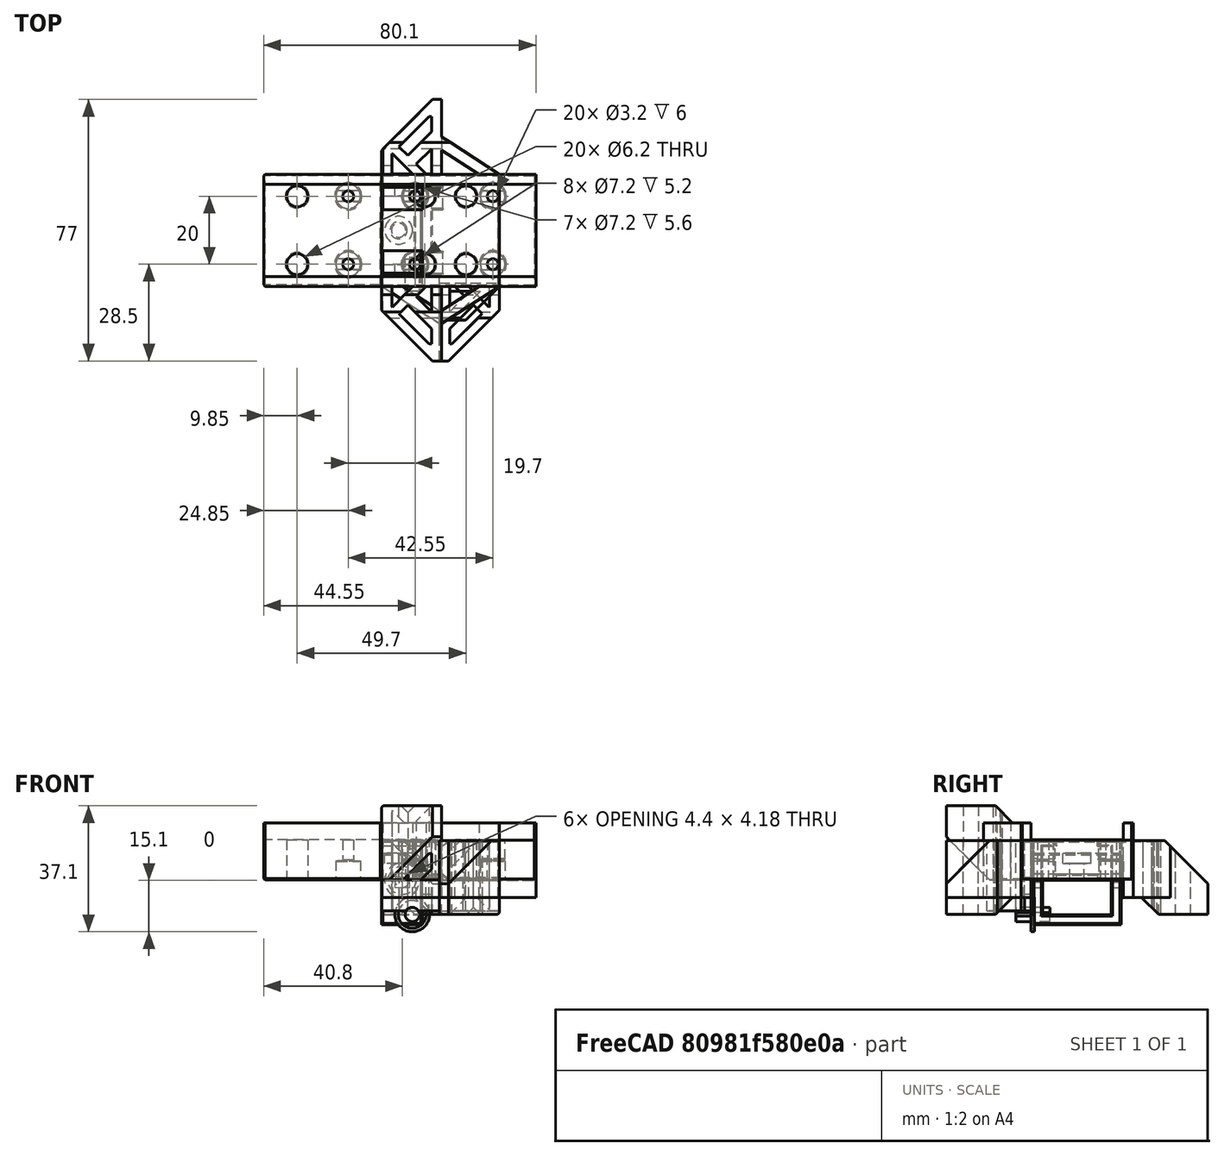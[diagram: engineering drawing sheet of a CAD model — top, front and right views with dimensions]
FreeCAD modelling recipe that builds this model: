
FCSTD DOCUMENT  (FreeCAD 0.18R14555 (Git shallow))
Label: bear-railt-mount
License: All rights reserved
LicenseURL: http://en.wikipedia.org/wiki/All_rights_reserved
objects: Part::Box×31, Part::Feature×25, Part::Cut×24, Part::Cylinder×22, Part::MultiFuse×16, Part::Chamfer×15, Part::MultiCommon×1
note: 134 computed .brp shape members not serialized (recipe doc carries the construction recipe); baked Part::Feature solids carry a one-line shape summary decoded from their .brp

FEATURE [Part::Box] Box  label="Cube"
  AttacherType = Attacher::AttachEngine3D
  Height = 2
  Length = 18
  Placement = pos=(0,-13,0) rot=(0,0,1;0rad)
  Width = 26
FEATURE [Part::Box] Box001  label="Cube001"
  AttacherType = Attacher::AttachEngine3D
  Height = 8
  Length = 10
  Placement = pos=(0,-13,0) rot=(0,0,1;0rad)
  Width = 26
FEATURE [Part::Cylinder] Cylinder
  Angle = 360
  AttacherType = Attacher::AttachEngine3D
  Height = 8
  Placement = pos=(5,0,0) rot=(0,0,1;0rad)
  Radius = 2.1
FEATURE [Part::Cylinder] Cylinder001
  Angle = 360
  AttacherType = Attacher::AttachEngine3D
  Height = 3
  Placement = pos=(5,0,5) rot=(0,0,1;0rad)
  Radius = 4.1
FEATURE [Part::Box] Box004  label="Cube004"
  AttacherType = Attacher::AttachEngine3D
  Height = 2
  Length = 3
  Placement = pos=(15,-6.1,0) rot=(0,0,1;0rad)
  Width = 12.2
FEATURE [Part::Box] Box006  label="Cube006"
  AttacherType = Attacher::AttachEngine3D
  Height = 20.2
  Length = 12
  Placement = pos=(0,-10.1,-10.1) rot=(0,0,1;0rad)
  Width = 20.2
FEATURE [Part::Box] Box007  label="Cube007"
  AttacherType = Attacher::AttachEngine3D
  Height = 25
  Length = 12
  Placement = pos=(0,-13,-13) rot=(0,0,1;0rad)
  Width = 26
FEATURE [Part::Cut] Cut002
  Base = -> Box007
  Tool = -> Box006
FEATURE [Part::Box] Box008  label="Cube008"
  AttacherType = Attacher::AttachEngine3D
  Height = 10
  Length = 12
  Placement = pos=(0,-6.05,4) rot=(0,0,1;0rad)
  Width = 12.1
FEATURE [Part::Cut] Cut003
  Base = -> Cut002
  Tool = -> Box008
FEATURE [Part::Cylinder] Cylinder004
  Angle = 360
  AttacherType = Attacher::AttachEngine3D
  Height = 38
  Placement = pos=(6,-18,4e-15) rot=(-1,0,0;1.5708rad)
  Radius = 2.1
FEATURE [Part::Cylinder] Cylinder005
  Angle = 360
  AttacherType = Attacher::AttachEngine3D
  Height = 38
  Placement = pos=(7.8,-18,4e-15) rot=(-1,0,0;1.5708rad)
  Radius = 0.5
FEATURE [Part::MultiFuse] Fusion002
  Shapes = -> [Cylinder004,Cylinder005]
FEATURE [Part::Cut] Cut004  label="node-rev-1-tmp"
  Base = -> Cut003
  Tool = -> Fusion002
FEATURE [Part::Box] Box009  label="Cube009"
  AttacherType = Attacher::AttachEngine3D
  Height = 16.8
  Length = 34.7
  Placement = pos=(0,-16.5,-5) rot=(0,0,1;0rad)
  Width = 33
FEATURE [Part::Box] Box010  label="Cube010"
  AttacherType = Attacher::AttachEngine3D
  Height = 5
  Length = 34.7
  Placement = pos=(0,-13.6,-5) rot=(0,0,1;0rad)
  Width = 27.2
FEATURE [Part::Cylinder] Cylinder006
  Angle = 360
  AttacherType = Attacher::AttachEngine3D
  Height = 12
  Placement = pos=(9.85,10,0) rot=(0,0,1;0rad)
  Radius = 1.6
FEATURE [Part::Cylinder] Cylinder007
  Angle = 360
  AttacherType = Attacher::AttachEngine3D
  Height = 12
  Placement = pos=(9.85,-10,0) rot=(0,0,1;0rad)
  Radius = 1.6
FEATURE [Part::Cylinder] Cylinder008
  Angle = 360
  AttacherType = Attacher::AttachEngine3D
  Height = 12
  Placement = pos=(24.85,10,0) rot=(0,0,1;0rad)
  Radius = 3.1
FEATURE [Part::Cylinder] Cylinder009
  Angle = 360
  AttacherType = Attacher::AttachEngine3D
  Height = 12
  Placement = pos=(24.85,-10,0) rot=(0,0,1;0rad)
  Radius = 3.1
FEATURE [Part::Cylinder] Cylinder010
  Angle = 360
  AttacherType = Attacher::AttachEngine3D
  Height = 6
  Placement = pos=(9.85,-10,6) rot=(0,0,1;0rad)
  Radius = 3.6
FEATURE [Part::Cylinder] Cylinder011
  Angle = 360
  AttacherType = Attacher::AttachEngine3D
  Height = 6
  Placement = pos=(9.85,10,6) rot=(0,0,1;0rad)
  Radius = 3.6
FEATURE [Part::Cylinder] Cylinder012
  Angle = 360
  AttacherType = Attacher::AttachEngine3D
  Height = 10
  Placement = pos=(9,-8,-10) rot=(1,0,0;1.5708rad)
  Radius = 2.1
FEATURE [Part::Cylinder] Cylinder013
  Angle = 360
  AttacherType = Attacher::AttachEngine3D
  Height = 10
  Placement = pos=(10.9,-8,-10) rot=(1,0,0;1.5708rad)
  Radius = 0.5
FEATURE [Part::Cylinder] Cylinder014
  Angle = 360
  AttacherType = Attacher::AttachEngine3D
  Height = 1
  Placement = pos=(9,-12.5,-10) rot=(1,0,0;1.5708rad)
  Radius = 5.1
FEATURE [Part::Cylinder] Cylinder015
  Angle = 360
  AttacherType = Attacher::AttachEngine3D
  Height = 1
  Placement = pos=(9,-12.5,-10) rot=(1,0,0;1.5708rad)
  Radius = 4.1
FEATURE [Part::Cut] Cut
  Base = -> Cylinder014
  Tool = -> Cylinder015
FEATURE [Part::Cylinder] Cylinder016
  Angle = 360
  AttacherType = Attacher::AttachEngine3D
  Height = 1
  Placement = pos=(12.9,-12.5,-10) rot=(1,0,0;1.5708rad)
  Radius = 0.5
FEATURE [Part::Cut] Cut007  label="side-hole-deco"
  Base = -> Cut
  Tool = -> Cylinder016
FEATURE [Part::MultiFuse] Fusion004  label="side-screw-hole"
  Shapes = -> [Cylinder012,Cylinder013]
FEATURE [Part::Cut] Cut007009
  Base = -> Box009
  Tool = -> Box010
FEATURE [Part::Box] Box011  label="Cube011"
  AttacherType = Attacher::AttachEngine3D
  Height = 20.8
  Length = 17.7
  Placement = pos=(17,-26.5,-9) rot=(0,0,1;0rad)
  Width = 11
FEATURE [Part::Box] Box012  label="Cube012"
  AttacherType = Attacher::AttachEngine3D
  Height = 10
  Length = 34.7
  Placement = pos=(0,-16.5,-9) rot=(0,0,1;0rad)
  Width = 2.9
FEATURE [Part::Feature] Body001
  shape: bbox 11 x 9 x 20 mm, 6 faces (baked)
FEATURE [Part::Feature] Body002
  Placement = pos=(0,0,5) rot=(0,0,1;0rad)
  shape: bbox 11 x 9 x 20 mm, 6 faces (baked)
FEATURE [Part::MultiFuse] Fusion004006
  Shapes = -> [Body002,Body001]
FEATURE [Part::Chamfer] Chamfer
  Base = -> Box011
  Edges = 1 edges r=10: [Edge5]
FEATURE [Part::Box] Box013  label="Cube013"
  AttacherType = Attacher::AttachEngine3D
  Height = 31
  Length = 10
  Placement = pos=(15,-33,-18) rot=(0,0,1;0rad)
  Width = 10
FEATURE [Part::Box] Box014  label="Cube014"
  AttacherType = Attacher::AttachEngine3D
  Height = 31
  Length = 10
  Placement = pos=(11,-26,-18) rot=(0,0,1;0rad)
  Width = 10
FEATURE [Part::Cut] Cut007010
  Base = -> Fusion004006
  Tool = -> Box013
FEATURE [Part::Cut] Cut007011
  Base = -> Cut007010
  Placement = pos=(-1,0,0) rot=(0,0,1;0rad)
  Tool = -> Box014
FEATURE [Part::Cut] Cut007012
  Base = -> Chamfer
  Tool = -> Cut007011
FEATURE [Part::MultiFuse] Fusion004007
  Shapes = -> [Cylinder011,Cylinder006,Cylinder007,Cylinder008,Cylinder009,Cylinder010]
FEATURE [Part::Cut] Cut007013  label="block-rev-tmp-1"
  Base = -> Cut007009
  Tool = -> Fusion004007
FEATURE [Part::MultiFuse] Fusion004008
  Shapes = -> [Box,Box001]
FEATURE [Part::Cut] Cut007014
  Base = -> Fusion004008
  Tool = -> Box004
FEATURE [Part::MultiFuse] Fusion
  Shapes = -> [Cylinder,Cylinder001]
FEATURE [Part::Cut] Cut007015  label="head-tail-rev-1"
  Base = -> Cut007014
  Tool = -> Fusion
FEATURE [Part::Box] Box015  label="Cube015"
  AttacherType = Attacher::AttachEngine3D
  Height = 16.8
  Length = 11.7
  Placement = pos=(20,-33.5,-5) rot=(0,0,1;0rad)
  Width = 16.9
FEATURE [Part::Box] Box016  label="Cube016"
  AttacherType = Attacher::AttachEngine3D
  Height = 16.8
  Length = 17.7
  Placement = pos=(17,-38.5,-5) rot=(0,0,1;0rad)
  Width = 24.9
FEATURE [Part::Chamfer] Chamfer001
  Base = -> Box016
  Edges = 1 edges r=15: [Edge5]
FEATURE [Part::Chamfer] Chamfer002
  Base = -> Box015
  Edges = 1 edges r=11: [Edge5]
FEATURE [Part::Cut] Cut007016
  Base = -> Chamfer001
  Tool = -> Chamfer002
FEATURE [Part::Box] Box017  label="Cube017"
  AttacherType = Attacher::AttachEngine3D
  Height = 16.8
  Length = 10
  Placement = pos=(13,-27,-5) rot=(0,0,1;0rad)
  Width = 10
FEATURE [Part::Box] Box018  label="Cube018"
  AttacherType = Attacher::AttachEngine3D
  Height = 16.8
  Length = 15
  Placement = pos=(40,-26,-5) rot=(0,0,1;0rad)
  Width = 18
FEATURE [Part::Box] Box019  label="Cube019"
  AttacherType = Attacher::AttachEngine3D
  Height = 16.8
  Length = 15
  Placement = pos=(40,-26,-5) rot=(0,0,1;0rad)
  Width = 18
FEATURE [Part::Chamfer] Chamfer003
  Base = -> Box018
  Edges = 1 edges r=10: [Edge1]
  Placement = pos=(-20,1,0) rot=(0,0,1;0rad)
FEATURE [Part::Chamfer] Chamfer004
  Base = -> Box019
  Edges = 1 edges r=14: [Edge1]
  Placement = pos=(-20,1,0) rot=(0,0,1;0rad)
FEATURE [Part::Cut] Cut007017
  Base = -> Chamfer003
  Tool = -> Chamfer004
FEATURE [Part::Box] Box020  label="Cube020"
  AttacherType = Attacher::AttachEngine3D
  Height = 16.8
  Length = 10
  Placement = pos=(13,-68,-5) rot=(0,0,1;0rad)
  Width = 12
FEATURE [Part::Chamfer] Chamfer005
  Base = -> Box020
  Edges = 1 edges r=9: [Edge3]
  Placement = pos=(4,38,0) rot=(0,0,1;0rad)
FEATURE [Part::Feature] Chamfer005001  label="Chamfer006"
  Placement = pos=(6,35,0) rot=(0,0,1;0rad)
  shape: bbox 10 x 12 x 16.8 mm, 7 faces (baked)
FEATURE [Part::Cut] Cut007018
  Base = -> Chamfer005
  Tool = -> Chamfer005001
FEATURE [Part::Box] Box021  label="Cube021"
  AttacherType = Attacher::AttachEngine3D
  Height = 16.8
  Length = 10
  Placement = pos=(15,-13.6,-5) rot=(0,0,1;0rad)
  Width = 10
FEATURE [Part::Cut] Cut007019
  Base = -> Cut007017
  Tool = -> Box021
FEATURE [Part::Chamfer] Chamfer005002
  Base = -> Box017
  Edges = 1 edges r=5: [Edge3]
  Placement = pos=(18,-5,0) rot=(0,0,1;0rad)
FEATURE [Part::Cut] Cut007020
  Base = -> Cut007019
  Tool = -> Chamfer005002
FEATURE [Part::MultiFuse] Fusion004009
  Shapes = -> [Cut007020,Cut007016,Cut007018]
FEATURE [Part::Feature] Fusion004009001  label="short-arm"
  shape: bbox 17.7 x 24.9 x 16.8 mm, 20 faces (baked)
FEATURE [Part::Feature] Fusion004009002  label="short-arm001"
  Placement = pos=(0,0,-5) rot=(0,0,1;0rad)
  shape: bbox 17.7 x 24.9 x 16.8 mm, 20 faces (baked)
FEATURE [Part::Box] Box022  label="Cube022"
  AttacherType = Attacher::AttachEngine3D
  Height = 0.2
  Length = 4
  Placement = pos=(1.6,-5,0) rot=(0,0,1;0rad)
  Width = 10
FEATURE [Part::Box] Box023  label="Cube023"
  AttacherType = Attacher::AttachEngine3D
  Height = 0.2
  Length = 4
  Placement = pos=(-5.6,-5,0) rot=(0,0,1;0rad)
  Width = 10
FEATURE [Part::Box] Box024  label="Cube024"
  AttacherType = Attacher::AttachEngine3D
  Height = 0.4
  Length = 8
  Placement = pos=(-4,-6.6,0) rot=(0,0,1;0rad)
  Width = 5
FEATURE [Part::Box] Box025  label="Cube025"
  AttacherType = Attacher::AttachEngine3D
  Height = 0.4
  Length = 8
  Placement = pos=(-4,1.6,0) rot=(0,0,1;0rad)
  Width = 5
FEATURE [Part::Cylinder] Cylinder017
  Angle = 360
  AttacherType = Attacher::AttachEngine3D
  Height = 10
  Radius = 3.7
FEATURE [Part::MultiFuse] Fusion004009004
  Shapes = -> [Box025,Box023,Box024,Box022]
FEATURE [Part::MultiCommon] Common  label="screw-hole-support"
  Placement = pos=(9.85,10,6) rot=(0,0,1;0rad)
  Shapes = -> [Cylinder017,Fusion004009004]
FEATURE [Part::Feature] Common001  label="screw-hole-support001"
  shape: bbox 7.4 x 7.4 x 0.4 mm, 10 faces (baked)
FEATURE [Part::Feature] Common002  label="screw-hole-support002"
  Placement = pos=(0,-20,0) rot=(0,0,1;0rad)
  shape: bbox 7.4 x 7.4 x 0.4 mm, 10 faces (baked)
FEATURE [Part::MultiFuse] Fusion004009005  label="block-rev-1"
  Shapes = -> [Common001,Common002,Cut007013]
FEATURE [Part::Box] Box026  label="Cube026"
  AttacherType = Attacher::AttachEngine3D
  Height = 6
  Length = 6
  Placement = pos=(12,-16.5,-10) rot=(0,0,1;0rad)
  Width = 2.9
FEATURE [Part::Box] Box027  label="Cube027"
  AttacherType = Attacher::AttachEngine3D
  Height = 16.8
  Length = 17
  Placement = pos=(0,-28,-5) rot=(0,0,1;0rad)
  Width = 12
FEATURE [Part::Box] Box028  label="Cube028"
  AttacherType = Attacher::AttachEngine3D
  Height = 16.8
  Length = 34
  Placement = pos=(-10.4225,-24.0104,-5) rot=(0,0,-1;0.575959rad)
  Width = 12
FEATURE [Part::Cut] Cut007021
  Base = -> Box027
  Tool = -> Box028
FEATURE [Part::Feature] Cut007021001  label="Cut007022"
  Placement = pos=(6,0,0) rot=(0,0,1;0rad)
  shape: bbox 17 x 11.51 x 16.8 mm, 6 faces (baked)
FEATURE [Part::Cut] Cut007021002
  Base = -> Cut007021
  Tool = -> Cut007021001
FEATURE [Part::Box] Box029  label="Cube029"
  AttacherType = Attacher::AttachEngine3D
  Height = 16
  Length = 36
  Placement = pos=(0,-20,-9) rot=(0,0,1;0rad)
  Width = 15
FEATURE [Part::Chamfer] Chamfer005004  label="cut"
  Base = -> Box029
  Edges = 1 edges r=9: [Edge10]
  Placement = pos=(0,-8,-12) rot=(0,0,1;0rad)
FEATURE [Part::Box] Box030  label="Cube030"
  AttacherType = Attacher::AttachEngine3D
  Height = 29
  Length = 39
  Placement = pos=(0,-41,27) rot=(0,0,1;0rad)
  Width = 38
FEATURE [Part::Chamfer] Chamfer005006
  Base = -> Box026
  Edges = 1 edges r=5: [Edge4]
FEATURE [Part::MultiFuse] Fusion004009006
  Shapes = -> [Chamfer005006,Fusion004009002,Cut007021002,Fusion004009001]
FEATURE [Part::Cut] Cut007021003
  Base = -> Fusion004009006
  Tool = -> Chamfer005004
FEATURE [Part::Chamfer] Chamfer005007
  Base = -> Box030
  Edges = 1 edges r=20: [Edge11]
  Placement = pos=(0,-15.6,-28) rot=(0,0,1;0rad)
FEATURE [Part::Cut] Cut007021004  label="arm-rev-1"
  Base = -> Cut007021003
  Tool = -> Chamfer005007
FEATURE [Part::Feature] Cut007021004001  label="arm-rev-002"
  shape: bbox 34.7 x 24.9 x 21.8 mm, 33 faces (baked)
FEATURE [Part::Feature] Fusion004009005001  label="block-rev-002"
  shape: bbox 34.7 x 33 x 16.8 mm, 40 faces (baked)
FEATURE [Part::MultiFuse] Fusion004009005002
  Shapes = -> [Cut007021004001,Fusion004009005001]
FEATURE [Part::Feature] Fusion004009005002002  label="block-rev-1-tmp"
  shape: bbox 34.7 x 33 x 16.8 mm, 40 faces (baked)
FEATURE [Part::Feature] Cut007015001  label="head-tail-rev-1-tmp"
  shape: bbox 18 x 26 x 8 mm, 15 faces (baked)
FEATURE [Part::Chamfer] Chamfer005010  label="head-tail-rev-1-exp"
  Base = -> Cut007015001
  Edges = 20 edges r=0.4: [Edge1,Edge2,Edge3,Edge4,Edge6,Edge7,Edge13,Edge15,Edge16,Edge17,Edge18,Edge24,Edge27,Edge28,Edge31,Edge32,Edge33,Edge34,Edge35,Edge36]
FEATURE [Part::Chamfer] Chamfer005012  label="block-12C-rev-1-exp"
  Base = -> Fusion004009005002002
  Edges = 12 edges r=0.4: [Edge23,Edge35,Edge36,Edge37,Edge38,Edge39,Edge40,Edge41,Edge45,Edge51,Edge53,Edge55]
FEATURE [Part::Feature] Chamfer005010_solid  label="head-tail-rev-1-exp (Solid)"
  shape: bbox 18 x 26 x 8 mm, 41 faces (baked)
FEATURE [Part::Feature] Chamfer005012_solid  label="block-rev-1-exp (Solid)"
  Placement = pos=(-1e-15,0,12) rot=(0,1,0;3.14159rad)
  shape: bbox 34.7 x 33 x 16.8 mm, 56 faces (baked)
FEATURE [Part::Feature] Fusion004009005002003  label="block-rev-003"
  shape: bbox 34.7 x 33 x 16.8 mm, 40 faces (baked)
FEATURE [Part::Feature] Cut007021004002  label="arm-rev-003"
  Placement = pos=(34.7,-5e-15,0) rot=(0,0,1;3.14159rad)
  shape: bbox 34.7 x 24.9 x 21.8 mm, 70 faces (baked)
FEATURE [Part::MultiFuse] Fusion004009005002004
  Shapes = -> [Fusion004009005002003,Cut007021004002]
FEATURE [Part::Feature] Fusion004009005002004001  label="Fusion004009005002005"
  shape: bbox 34.7 x 55 x 21.8 mm, 63 faces (baked)
FEATURE [Part::Chamfer] Chamfer005013
  Base = -> Fusion004009005002004001
  Edges = 9 edges r=0.4: [Edge11,Edge75,Edge77,Edge85,Edge86,Edge87,Edge93,Edge102,Edge106]
FEATURE [Part::Feature] Chamfer005013001  label="block-w-arm-rev-exp"
  Placement = pos=(0,1e-15,12) rot=(1,0,0;3.14159rad)
  shape: bbox 34.7 x 55 x 21.8 mm, 75 faces (baked)
FEATURE [Part::Box] Box031  label="Cube031"
  AttacherType = Attacher::AttachEngine3D
  Height = 11.9
  Length = 45.4
  Placement = pos=(0,-16.5,0) rot=(0,0,1;0rad)
  Width = 33
FEATURE [Part::Box] Box032  label="Cube032"
  AttacherType = Attacher::AttachEngine3D
  Height = 5
  Length = 45.4
  Placement = pos=(0,-16.5,-5) rot=(0,0,1;0rad)
  Width = 2.9
FEATURE [Part::Box] Box033  label="Cube033"
  AttacherType = Attacher::AttachEngine3D
  Height = 5
  Length = 45.4
  Placement = pos=(0,13.6,-5) rot=(0,0,1;0rad)
  Width = 2.9
FEATURE [Part::Cylinder] Cylinder018
  Angle = 360
  AttacherType = Attacher::AttachEngine3D
  Height = 15
  Placement = pos=(12.7,-10,0) rot=(0,0,1;0rad)
  Radius = 3.1
FEATURE [Part::Cylinder] Cylinder019
  Angle = 360
  AttacherType = Attacher::AttachEngine3D
  Height = 6
  Placement = pos=(32.7,-10,0) rot=(0,0,1;0rad)
  Radius = 3.6
FEATURE [Part::Cylinder] Cylinder020
  Angle = 360
  AttacherType = Attacher::AttachEngine3D
  Height = 6
  Placement = pos=(32.7,10,0) rot=(0,0,1;0rad)
  Radius = 3.6
FEATURE [Part::Cylinder] Cylinder021
  Angle = 360
  AttacherType = Attacher::AttachEngine3D
  Height = 15
  Placement = pos=(12.7,10,0) rot=(0,0,1;0rad)
  Radius = 3.1
FEATURE [Part::MultiFuse] Fusion004009005002004002
  Shapes = -> [Cylinder021,Cylinder018]
FEATURE [Part::Cut] Cut007021004003
  Base = -> Box031
  Tool = -> Fusion004009005002004002
FEATURE [Part::Cylinder] Cylinder022
  Angle = 360
  AttacherType = Attacher::AttachEngine3D
  Height = 15
  Placement = pos=(32.7,-10,0) rot=(0,0,1;0rad)
  Radius = 1.6
FEATURE [Part::Cylinder] Cylinder023
  Angle = 360
  AttacherType = Attacher::AttachEngine3D
  Height = 15
  Placement = pos=(32.7,10,0) rot=(0,0,1;0rad)
  Radius = 1.6
FEATURE [Part::MultiFuse] Fusion004009005002004003
  Shapes = -> [Cylinder022,Cylinder023]
FEATURE [Part::Cut] Cut007021004004
  Base = -> Cut007021004003
  Tool = -> Fusion004009005002004003
FEATURE [Part::MultiFuse] Fusion004009005002004004
  Placement = pos=(0,0,6) rot=(0,0,1;0rad)
  Shapes = -> [Cylinder019,Cylinder020]
FEATURE [Part::Cut] Cut007021004005
  Base = -> Cut007021004004
  Tool = -> Fusion004009005002004004
FEATURE [Part::Feature] Common003  label="screw-hole-support003"
  Placement = pos=(22.85,0,0) rot=(0,0,1;0rad)
  shape: bbox 7.4 x 7.4 x 0.4 mm, 10 faces (baked)
FEATURE [Part::Feature] Common004  label="screw-hole-support004"
  Placement = pos=(22.85,-20,0) rot=(0,0,1;0rad)
  shape: bbox 7.4 x 7.4 x 0.4 mm, 10 faces (baked)
FEATURE [Part::MultiFuse] Fusion004009005002004005  label="block-12h-rev-1"
  Shapes = -> [Box032,Box033,Common003,Cut007021004005,Common004]
FEATURE [Part::Feature] Fusion004009005002004005001  label="block-12h-rev-002"
  shape: bbox 45.4 x 33 x 16.9 mm, 40 faces (baked)
FEATURE [Part::Chamfer] Chamfer005013002
  Base = -> Fusion004009005002004005001
  Edges = 12 edges r=0.4: [Edge1,Edge2,Edge3,Edge4,Edge5,Edge6,Edge7,Edge8,Edge101,Edge102,Edge103,Edge104]
  Placement = pos=(0,1e-15,12) rot=(1,0,0;3.14159rad)
FEATURE [Part::Feature] Chamfer005013002_solid  label="block-12h-rev-1-exp"
  shape: bbox 45.4 x 33 x 16.9 mm, 56 faces (baked)
FEATURE [Part::Feature] Fusion004005001  label="node-rev-1-w-aliner"
  shape: bbox 12 x 27 x 25 mm, 28 faces (baked)
FEATURE [Part::Chamfer] Chamfer005013003  label="node-rev-1"
  Base = -> Cut004
  Edges = 25 edges r=0.4: [Edge1,Edge3,Edge4,Edge5,Edge6,Edge7,Edge9,Edge10,Edge11,Edge12,Edge14,Edge15,Edge16,Edge18,Edge21,Edge26,Edge27,Edge32,Edge34,Edge36,Edge38,Edge39,Edge43,Edge44,Edge45]
FEATURE [Part::Feature] Chamfer005013003001  label="node-rev-1-exp"
  shape: bbox 12 x 26 x 25 mm, 50 faces (baked)
FEATURE [Part::Feature] Fusion004009005002004005002  label="Fusion004009005002004005"
  shape: bbox 34.7 x 55 x 21.8 mm, 63 faces (baked)
